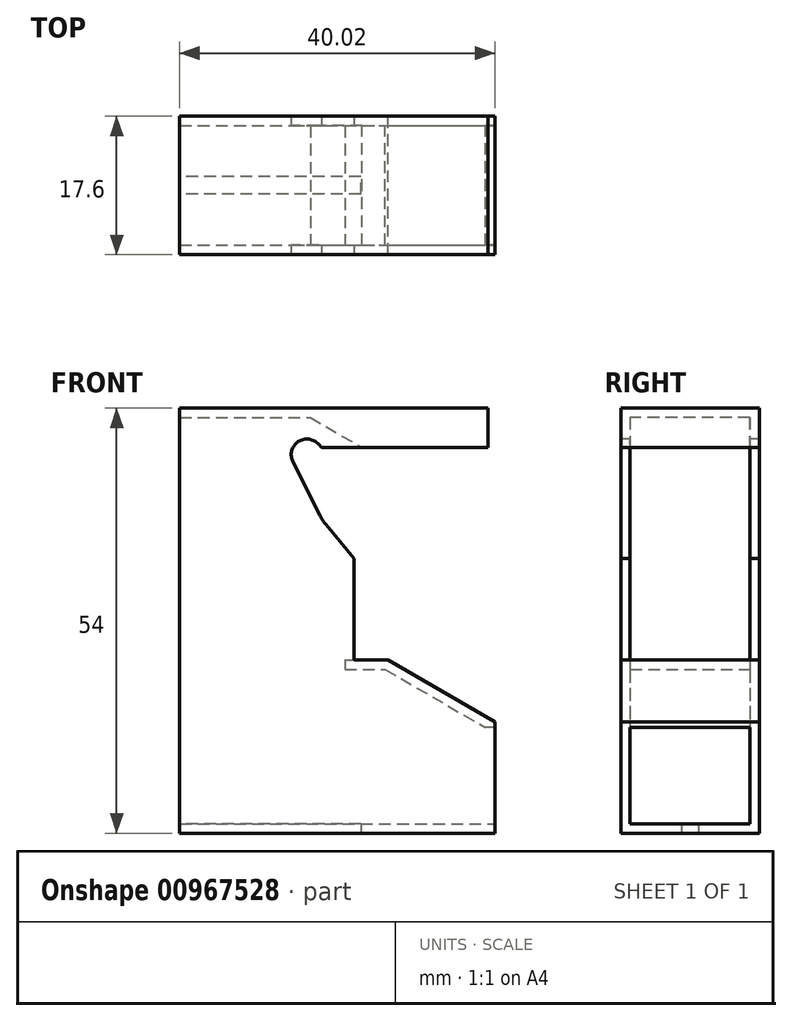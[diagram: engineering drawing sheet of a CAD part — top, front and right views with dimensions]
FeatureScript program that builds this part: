
annotation { "Feature Type Name" : "Feature", "Feature Type Description" : "" }
export const myFeature = defineFeature(function(context is Context, id is Id, definition is map)
    precondition{}
    {
        {
            var Q0;
            Q0=qCreatedBy(makeId("Front.planeOp"),FACE);
            var sketch = newSketch(context, id + "F0", { "sketchPlane" : qUnion([Q0])});
            skLineSegment(sketch, "E0", {"start": v(-40.02, 0) * mm, "end": v(0, 0) * mm});
            skCircle(sketch, "E1", {"center": v(-24.15, 48.7) * mm, "radius": 2.3 * mm});
            skLineSegment(sketch, "E2", {"start": v(-40.02, 54) * mm, "end": v(-17.85, 54) * mm});
            skLineSegment(sketch, "E3", {"start": v(-17.85, 54) * mm, "end": v(-17.85, 49) * mm, "construction": true});
            skLineSegment(sketch, "E4", {"start": v(-40.02, 54) * mm, "end": v(-40.02, 0) * mm});
            skLineSegment(sketch, "E5", {"start": v(-17.85, 22) * mm, "end": v(-13.6, 22) * mm});
            skLineSegment(sketch, "E6", {"start": v(-13.6, 22) * mm, "end": v(0, 14.15) * mm});
            skLineSegment(sketch, "E7", {"start": v(0, 14.15) * mm, "end": v(0, 0) * mm});
            skLineSegment(sketch, "E8", {"start": v(-13.6, 22) * mm, "end": v(4.03, 22) * mm, "construction": true});
            skLineSegment(sketch, "E9", {"start": v(-17.85, 54) * mm, "end": v(-0.85, 54) * mm});
            skLineSegment(sketch, "E10", {"start": v(-0.85, 54) * mm, "end": v(-0.85, 49) * mm});
            skLineSegment(sketch, "E11", {"start": v(-0.85, 49) * mm, "end": v(-17.85, 49) * mm});
            skLineSegment(sketch, "E12", {"start": v(-17.85, 49) * mm, "end": v(-17.85, 22) * mm});
            skSolve(sketch);
        }
        {
            var Q0;
            Q0=makeQuery(id+"F0.imprint","IMPRINT",FACE,{"disambiguationData":[TD([[makeQuery(id+"F0.imprint","IMPRINT",EDGE,{"derivedFrom":sQuery(id+"F0.wireOp",EDGE,"E0")}),1.0]])]});
            var Q1;
            Q1=makeQuery(id+"F0.imprint","IMPRINT",FACE,{"disambiguationData":[TD([[makeQuery(id+"F0.imprint","IMPRINT",EDGE,{"derivedFrom":sQuery(id+"F0.wireOp",EDGE,"zBYFPqKn-hqMi-nJUF-mnPQ-bn6k6F0ZCsce")}),1.0]])]});
            var Q2;
            Q2=makeQuery(id+"F0.imprint","IMPRINT",FACE,{"disambiguationData":[TD([[makeQuery(id+"F0.imprint","IMPRINT",EDGE,{"derivedFrom":sQuery(id+"F0.wireOp",EDGE,"E1")}),1.0]])]});
            extrude(context, id + "F1", {"entities" : qUnion([Q0, Q1, Q2]), "depth" : 17.6 * mm, "offsetDistance" : 25 * mm, "symmetric" : true});
        }
        {
            var Q0;
            Q0=makeQuery(id+"F1.opExtrude","SWEPT_FACE",FACE,{"disambiguationData":[OSD([sQuery(id+"F0.wireOp",EDGE,"E4")])]});
            shell(context, id + "F2", {"entities" : qUnion([Q0]), "thickness" : 1.2 * mm});
        }
        {
            var Q0;
            Q0=makeQuery(id+"F2.opShell","OFFSET_FACE",FACE,{"disambiguationData":[OSD([sQuery(id+"F0.wireOp",EDGE,"E10")])]});
            var Q1;
            Q1=makeQuery(id+"F1.opExtrude","SWEPT_FACE",FACE,{"disambiguationData":[OSD([sQuery(id+"F0.wireOp",EDGE,"E10")])]});
            extrude(context, id + "F3", {"entities" : qUnion([Q0]), "operationType" : NewBodyOperationType.REMOVE, "endBound" : BoundingType.UP_TO_SURFACE, "oppositeDirection" : true, "depth" : 25 * mm, "endBoundEntityFace" : qUnion([Q1]), "offsetDistance" : 25 * mm});
        }
        {
            var Q0;
            {var subQ0=sQuery(id+"F0.wireOp",EDGE,"E11");Q0=makeQuery(id+"F3.boolean.opBoolean","MERGE",FACE,{"derivedFrom":[makeQuery(id+"F2.opShell","OFFSET_FACE",FACE,{"disambiguationData":[OSD([subQ0])]})],"fromTools":[makeQuery(id+"F3.opExtrude","SWEPT_FACE",FACE,{"disambiguationData":[OSD([sQuery(id+"F0.wireOp",EDGE,"E10"),subQ0])]})]});}
            var Q1;
            Q1=makeQuery(id+"F1.opExtrude","SWEPT_FACE",FACE,{"disambiguationData":[OSD([sQuery(id+"F0.wireOp",EDGE,"E5")])]});
            extrude(context, id + "F4", {"entities" : qUnion([Q0]), "operationType" : NewBodyOperationType.REMOVE, "endBound" : BoundingType.UP_TO_SURFACE, "oppositeDirection" : true, "depth" : 25 * mm, "endBoundEntityFace" : qUnion([Q1]), "offsetDistance" : 25 * mm});
        }
        {
            var Q0;
            Q0=makeQuery(id+"F2.opShell","OFFSET_FACE",FACE,{"disambiguationData":[OSD([sQuery(id+"F0.wireOp",EDGE,"E7")])]});
            var Q1;
            Q1=makeQuery(id+"F1.opExtrude","SWEPT_FACE",FACE,{"disambiguationData":[OSD([sQuery(id+"F0.wireOp",EDGE,"E7")])]});
            extrude(context, id + "F5", {"entities" : qUnion([Q0]), "operationType" : NewBodyOperationType.REMOVE, "endBound" : BoundingType.UP_TO_SURFACE, "oppositeDirection" : true, "depth" : 25 * mm, "endBoundEntityFace" : qUnion([Q1]), "offsetDistance" : 25 * mm});
        }
        {
            var Q0;
            Q0=makeQuery(id+"F1.opExtrude","SWEPT_FACE",FACE,{"disambiguationData":[OSD([sQuery(id+"F0.wireOp",EDGE,"E0")])]});
            var sketch = newSketch(context, id + "F6", { "sketchPlane" : qUnion([Q0])});
            skLineSegment(sketch, "E13.bottom", {"start": v(-17.02, 1.1) * mm, "end": v(-40.02, 1.1) * mm});
            skLineSegment(sketch, "E13.top", {"start": v(-17.02, -1.1) * mm, "end": v(-40.02, -1.1) * mm});
            skLineSegment(sketch, "E13.left", {"start": v(-17.02, 1.1) * mm, "end": v(-17.02, -1.1) * mm});
            skLineSegment(sketch, "E13.right", {"start": v(-40.02, 1.1) * mm, "end": v(-40.02, -1.1) * mm});
            skPoint(sketch, "E13.middle", {"position": v(-28.52, 0) * mm});
            skPoint(sketch, "E13.middle.positionSnap0", {"position": v(-40.02, 0) * mm});
            skPoint(sketch, "E13.centerSnap0", {"position": v(-40.02, 0) * mm});
            skSolve(sketch);
        }
        {
            var Q0;
            Q0=makeQuery(id+"F6.imprint","IMPRINT",FACE,{"disambiguationData":[TD([[makeQuery(id+"F6.imprint","IMPRINT",EDGE,{"derivedFrom":sQuery(id+"F6.wireOp",EDGE,"E13.bottom")}),1.0]])]});
            var Q1;
            {var subQ0=sQuery(id+"F0.wireOp",EDGE,"E0");Q1=makeQuery(id+"F5.boolean.opBoolean","MERGE",FACE,{"derivedFrom":[makeQuery(id+"F2.opShell","OFFSET_FACE",FACE,{"disambiguationData":[OSD([subQ0])]})],"fromTools":[makeQuery(id+"F5.opExtrude","SWEPT_FACE",FACE,{"disambiguationData":[OSD([subQ0,sQuery(id+"F0.wireOp",EDGE,"E7")])]})]});}
            extrude(context, id + "F7", {"entities" : qUnion([Q0]), "operationType" : NewBodyOperationType.REMOVE, "endBound" : BoundingType.UP_TO_SURFACE, "oppositeDirection" : true, "depth" : 25 * mm, "endBoundEntityFace" : qUnion([Q1]), "offsetDistance" : 25 * mm});
        }
        {
            var Q0;
            Q0=makeQuery(id+"F1.opExtrude","CAP_FACE",FACE,{"disambiguationData":[OSD([sQuery(id+"F0.wireOp",EDGE,"E0"),sQuery(id+"F0.wireOp",EDGE,"E2"),sQuery(id+"F0.wireOp",EDGE,"E4"),sQuery(id+"F0.wireOp",EDGE,"E5"),sQuery(id+"F0.wireOp",EDGE,"E6"),sQuery(id+"F0.wireOp",EDGE,"E7"),sQuery(id+"F0.wireOp",EDGE,"E9"),sQuery(id+"F0.wireOp",EDGE,"E10"),sQuery(id+"F0.wireOp",EDGE,"E11"),sQuery(id+"F0.wireOp",EDGE,"E12")])],"isStart":false});
            var sketch = newSketch(context, id + "F8", { "sketchPlane" : qUnion([Q0])});
            skArc(sketch, "E14", {"start": v(-17.85, 49) * mm, "mid": v(-22.48, 45.16) * mm, "end": v(-21.45, 39.23) * mm});
            skPoint(sketch, "E15.0", {"position": v(-17.85, 49) * mm});
            skLineSegment(sketch, "E16", {"start": v(-21.45, 39.23) * mm, "end": v(-17.85, 34.94) * mm});
            skArc(sketch, "E17", {"start": v(-22.34, 49.4) * mm, "mid": v(-24.97, 49.74) * mm, "end": v(-25.64, 47.18) * mm});
            skLineSegment(sketch, "E18", {"start": v(-22.34, 49.4) * mm, "end": v(-22, 49) * mm});
            skLineSegment(sketch, "E19", {"start": v(-25.64, 47.18) * mm, "end": v(-22.21, 40.38) * mm});
            skLineSegment(sketch, "E20", {"start": v(-17.85, 49) * mm, "end": v(-22, 49) * mm});
            skLineSegment(sketch, "E21", {"start": v(-17.85, 49) * mm, "end": v(-17.85, 34.94) * mm});
            skSolve(sketch);
        }
        {
            var Q0;
            Q0=makeQuery(id+"F8.imprint","IMPRINT",FACE,{"disambiguationData":[TD([[makeQuery(id+"F8.imprint","IMPRINT",EDGE,{"derivedFrom":sQuery(id+"F8.wireOp",EDGE,"E17")}),1.0]])]});
            var Q1;
            {var subQ3=sQuery(id+"F8.wireOp",EDGE,"E16");Q1=makeQuery(id+"F8.imprint","IMPRINT",FACE,{"disambiguationData":[TD([[makeQuery(id+"F8.imprint","IMPRINT",EDGE,{"derivedFrom":subQ3}),1.0]])]});}
            var Q2;
            Q2=makeQuery(id+"F1.opExtrude","CAP_FACE",FACE,{"disambiguationData":[OSD([sQuery(id+"F0.wireOp",EDGE,"E0"),sQuery(id+"F0.wireOp",EDGE,"E2"),sQuery(id+"F0.wireOp",EDGE,"E4"),sQuery(id+"F0.wireOp",EDGE,"E5"),sQuery(id+"F0.wireOp",EDGE,"E6"),sQuery(id+"F0.wireOp",EDGE,"E7"),sQuery(id+"F0.wireOp",EDGE,"E9"),sQuery(id+"F0.wireOp",EDGE,"E10"),sQuery(id+"F0.wireOp",EDGE,"E11"),sQuery(id+"F0.wireOp",EDGE,"E12")])],"isStart":true});
            extrude(context, id + "F9", {"entities" : qUnion([Q0, Q1]), "operationType" : NewBodyOperationType.REMOVE, "endBound" : BoundingType.UP_TO_SURFACE, "oppositeDirection" : true, "depth" : 25 * mm, "endBoundEntityFace" : qUnion([Q2]), "offsetDistance" : 25 * mm});
        }
        {
            var Q0;
            Q0=makeQuery(id+"F1.opExtrude","SWEPT_FACE",FACE,{"disambiguationData":[OSD([sQuery(id+"F0.wireOp",EDGE,"E10")])]});
            var sketch = newSketch(context, id + "F10", { "sketchPlane" : qUnion([Q0])});
            skLineSegment(sketch, "E22.bottom", {"start": v(-7.6, 52.8) * mm, "end": v(7.6, 52.8) * mm});
            skLineSegment(sketch, "E22.top", {"start": v(-7.6, 49) * mm, "end": v(7.6, 49) * mm});
            skLineSegment(sketch, "E22.left", {"start": v(-7.6, 52.8) * mm, "end": v(-7.6, 49) * mm});
            skLineSegment(sketch, "E22.right", {"start": v(7.6, 52.8) * mm, "end": v(7.6, 49) * mm});
            skSolve(sketch);
        }
        {
            var Q0;
            Q0=makeQuery(id+"F10.imprint","IMPRINT",FACE,{"disambiguationData":[TD([[makeQuery(id+"F10.imprint","IMPRINT",EDGE,{"derivedFrom":sQuery(id+"F10.wireOp",EDGE,"E22.bottom")}),-1.0]])]});
            extrude(context, id + "F11", {"entities" : qUnion([Q0]), "operationType" : NewBodyOperationType.ADD, "oppositeDirection" : true, "depth" : 25 * mm, "offsetDistance" : 25 * mm});
        }
        {
            var Q0;
            Q0=makeQuery(id+"F11.opExtrude","CAP_EDGE",EDGE,{"disambiguationData":[OSD([sQuery(id+"F10.wireOp",EDGE,"E22.top")])],"isStart":false});
            chamfer(context, id + "F12", {"entities" : qUnion([Q0]), "chamferType" : ChamferType.OFFSET_ANGLE, "width" : 9 * mm, "oppositeDirection" : false, "angle" : 30 * degree, "tangentPropagation" : true});
        }
    });
